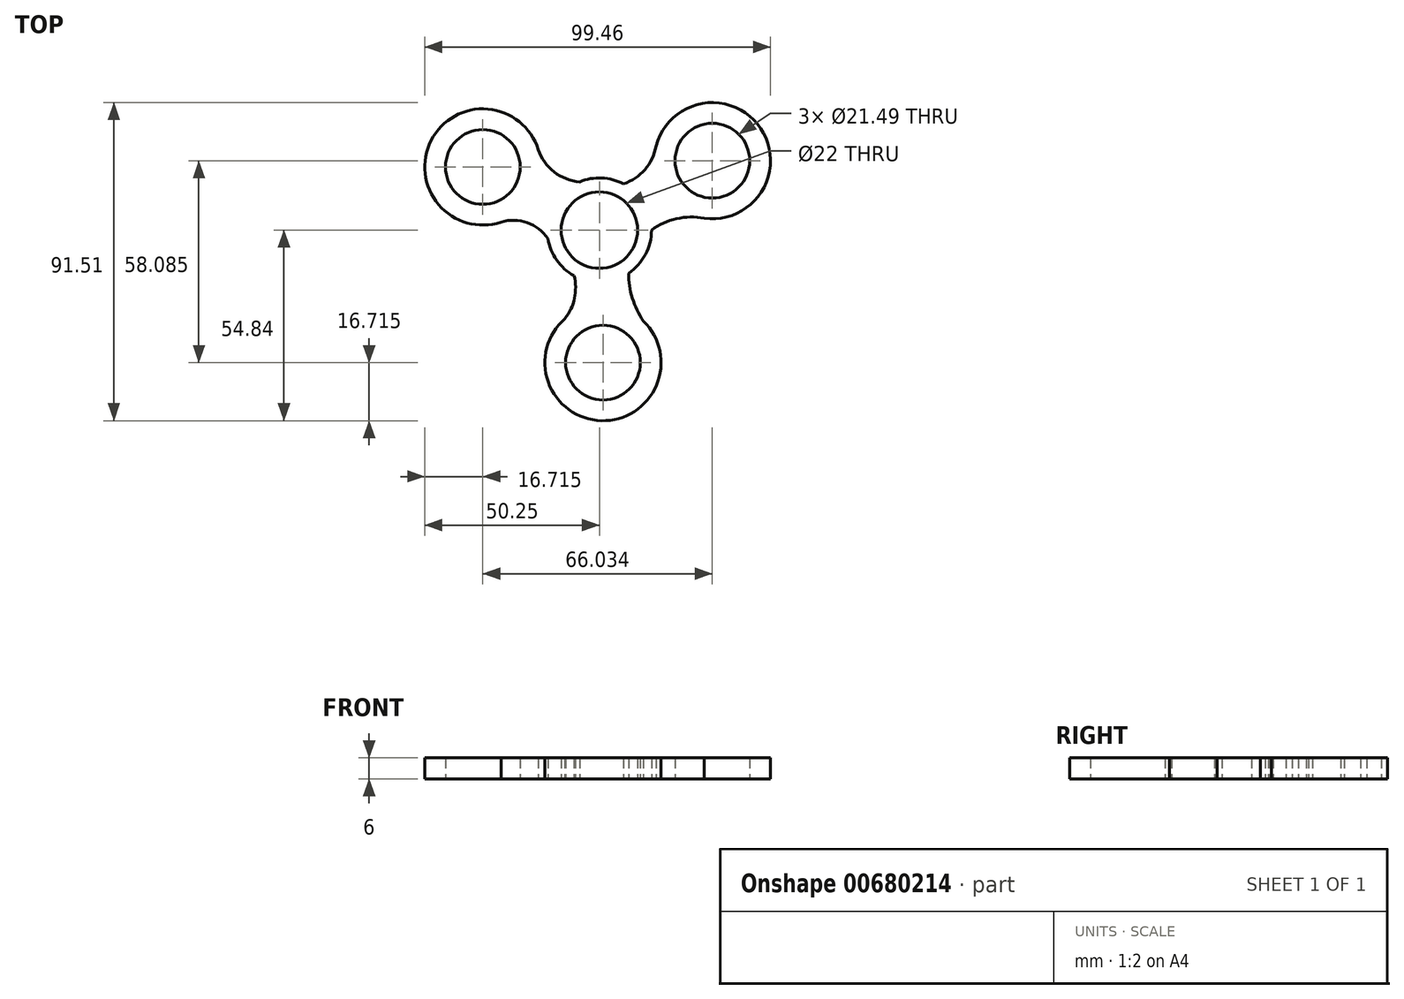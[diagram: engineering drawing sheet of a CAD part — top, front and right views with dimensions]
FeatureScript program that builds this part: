
annotation { "Feature Type Name" : "Feature", "Feature Type Description" : "" }
export const myFeature = defineFeature(function(context is Context, id is Id, definition is map)
    precondition{}
    {
        {
            var Q0;
            Q0=qCreatedBy(makeId("Top.planeOp"),FACE);
            var sketch = newSketch(context, id + "F0", { "sketchPlane" : qUnion([Q0])});
            skCircle(sketch, "E0", {"center": v(0, 0) * mm, "radius": 11 * mm});
            skCircle(sketch, "E1", {"center": v(0, 0) * mm, "radius": 15 * mm});
            skCircle(sketch, "E2", {"center": v(-33.54, 18.16) * mm, "radius": 10.74 * mm});
            skCircle(sketch, "E3", {"center": v(-33.54, 18.16) * mm, "radius": 16.71 * mm});
            skCircle(sketch, "E4.1.2", {"center": v(1.04, -38.12) * mm, "radius": 16.71 * mm});
            skCircle(sketch, "E4.1.3", {"center": v(1.04, -38.12) * mm, "radius": 10.74 * mm});
            skCircle(sketch, "E4.2.2", {"center": v(32.5, 19.96) * mm, "radius": 16.71 * mm});
            skCircle(sketch, "E4.2.3", {"center": v(32.5, 19.96) * mm, "radius": 10.74 * mm});
            skArc(sketch, "E5", {"start": v(-17.58, 23.14) * mm, "mid": v(-13.02, 16.75) * mm, "end": v(-5.71, 13.87) * mm});
            skArc(sketch, "E6", {"start": v(-14.8, -2.47) * mm, "mid": v(-20.77, 2.14) * mm, "end": v(-28.31, 2.29) * mm});
            skArc(sketch, "E7", {"start": v(6.96, 13.29) * mm, "mid": v(13.1, 17.44) * mm, "end": v(16.32, 24.13) * mm});
            skArc(sketch, "E8", {"start": v(30.13, 3.42) * mm, "mid": v(22.21, 3.27) * mm, "end": v(15, 0) * mm});
            skArc(sketch, "E9", {"start": v(8.39, -12.44) * mm, "mid": v(9.49, -19.62) * mm, "end": v(12.68, -26.14) * mm});
            skArc(sketch, "E10", {"start": v(-9.9, -25.5) * mm, "mid": v(-7.17, -19.6) * mm, "end": v(-7.3, -13.1) * mm});
            skSolve(sketch);
        }
        {
            var Q0;
            Q0=makeQuery(id+"F0.imprint","IMPRINT",FACE,{"disambiguationData":[TD([[makeQuery(id+"F0.imprint","IMPRINT",EDGE,{"derivedFrom":sQuery(id+"F0.wireOp",EDGE,"E2")}),-1.0]])]});
            var Q1;
            {var subQ0=sQuery(id+"F0.wireOp",EDGE,"E5");Q1=makeQuery(id+"F0.imprint","IMPRINT",FACE,{"disambiguationData":[TD([[makeQuery(id+"F0.imprint","IMPRINT",EDGE,{"derivedFrom":subQ0}),-1.0]])]});}
            var Q2;
            Q2=makeQuery(id+"F0.imprint","IMPRINT",FACE,{"disambiguationData":[TD([[makeQuery(id+"F0.imprint","IMPRINT",EDGE,{"derivedFrom":sQuery(id+"F0.wireOp",EDGE,"E0")}),-1.0]])]});
            var Q3;
            Q3=makeQuery(id+"F0.imprint","IMPRINT",FACE,{"disambiguationData":[TD([[makeQuery(id+"F0.imprint","IMPRINT",EDGE,{"derivedFrom":sQuery(id+"F0.wireOp",EDGE,"E4.2.3")}),-1.0]])]});
            var Q4;
            {var subQ0=sQuery(id+"F0.wireOp",EDGE,"E7");var subQ1=sQuery(id+"F0.wireOp",EDGE,"E1");var subQ2=makeQuery(id+"F0.imprint","INTERSECT",VERTEX,{"derivedFrom":[subQ1,subQ0]});Q4=makeQuery(id+"F0.imprint","IMPRINT",FACE,{"disambiguationData":[TD([[makeQuery(id+"F0.imprint","IMPRINT",EDGE,{"disambiguationData":[TD([[subQ2,1.0]])],"derivedFrom":subQ1}),-1.0]])]});}
            var Q5;
            {var subQ0=sQuery(id+"F0.wireOp",EDGE,"E9");Q5=makeQuery(id+"F0.imprint","IMPRINT",FACE,{"disambiguationData":[TD([[makeQuery(id+"F0.imprint","IMPRINT",EDGE,{"derivedFrom":subQ0}),-1.0]])]});}
            var Q6;
            Q6=makeQuery(id+"F0.imprint","IMPRINT",FACE,{"disambiguationData":[TD([[makeQuery(id+"F0.imprint","IMPRINT",EDGE,{"derivedFrom":sQuery(id+"F0.wireOp",EDGE,"E4.1.3")}),-1.0]])]});
            extrude(context, id + "F1", {"entities" : qUnion([Q0, Q1, Q2, Q3, Q4, Q5, Q6]), "depth" : 6 * mm, "offsetDistance" : 25 * mm});
        }
    });
